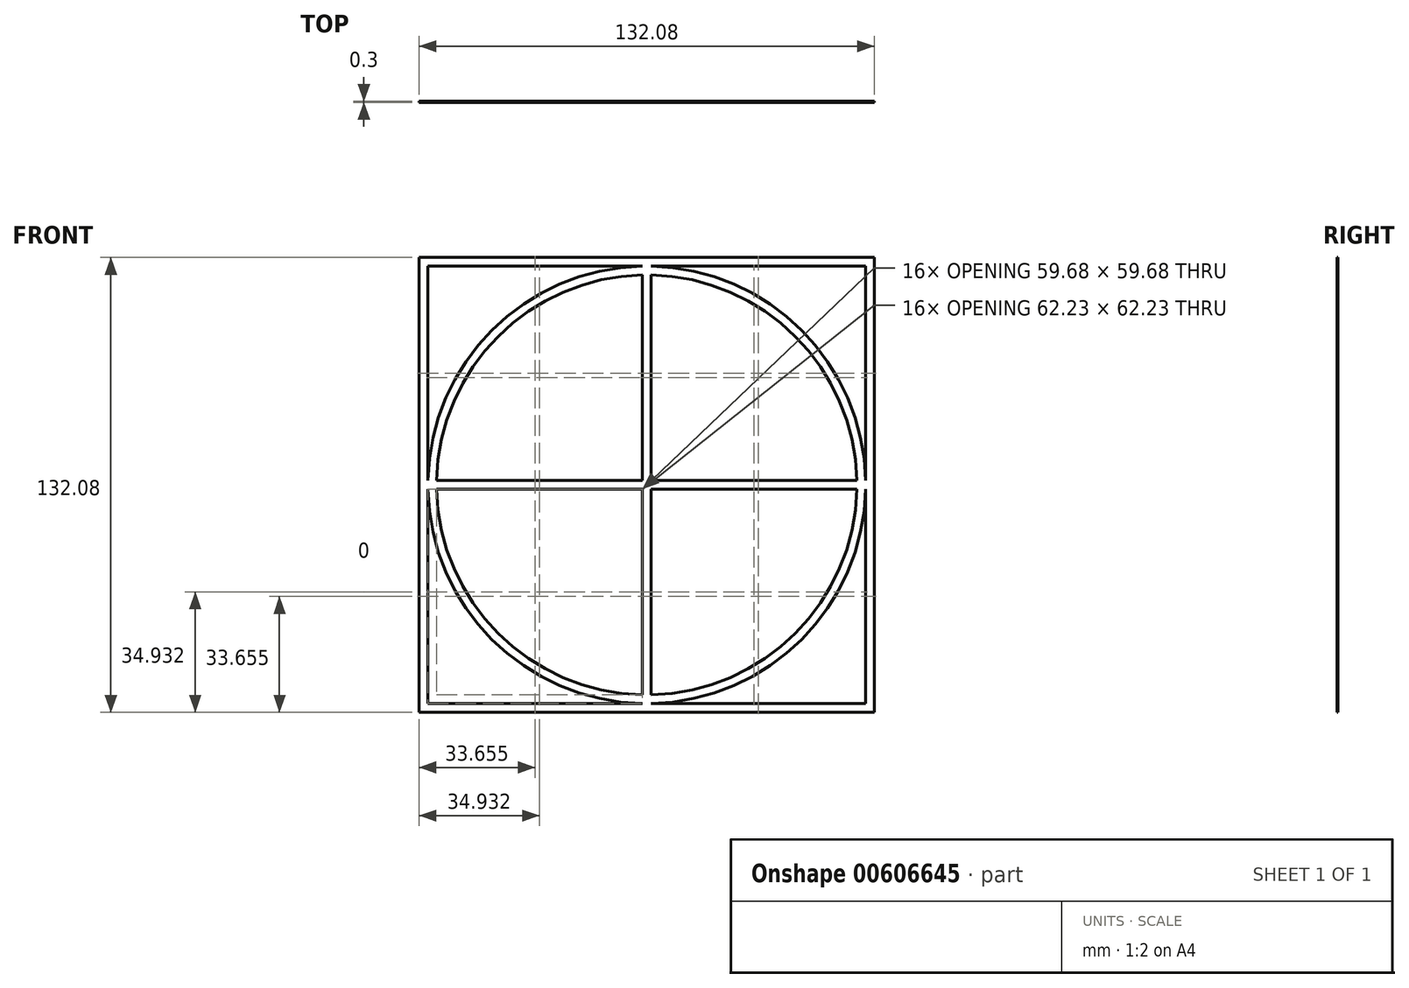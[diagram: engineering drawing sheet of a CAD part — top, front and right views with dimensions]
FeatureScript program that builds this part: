
annotation { "Feature Type Name" : "Feature", "Feature Type Description" : "" }
export const myFeature = defineFeature(function(context is Context, id is Id, definition is map)
    precondition{}
    {
        {
            var Q0;
            Q0=qCreatedBy(makeId("Front.planeOp"),FACE);
            var sketch = newSketch(context, id + "F0", { "sketchPlane" : qUnion([Q0])});
            skLineSegment(sketch, "E0.bottom", {"start": v(63.5, 63.5) * mm, "end": v(1.27, 63.5) * mm});
            skLineSegment(sketch, "E0.left", {"start": v(63.5, 63.5) * mm, "end": v(63.5, 1.27) * mm});
            skLineSegment(sketch, "E1.top", {"start": v(63.5, -63.5) * mm, "end": v(1.27, -63.5) * mm});
            skLineSegment(sketch, "E1.left", {"start": v(63.5, -1.27) * mm, "end": v(63.5, -63.5) * mm});
            skLineSegment(sketch, "E2.bottom", {"start": v(-1.27, -63.5) * mm, "end": v(-63.5, -63.5) * mm});
            skLineSegment(sketch, "E2.right", {"start": v(-63.5, -63.5) * mm, "end": v(-63.5, -1.27) * mm});
            skLineSegment(sketch, "E3.bottom", {"start": v(-1.27, 63.5) * mm, "end": v(-63.5, 63.5) * mm});
            skLineSegment(sketch, "E3.right", {"start": v(-63.5, 63.5) * mm, "end": v(-63.5, 1.27) * mm});
            skPoint(sketch, "E0.right.end.orphan", {"position": v(0, 0) * mm});
            skLineSegment(sketch, "E4.0", {"start": v(63.5, 1.27) * mm, "end": v(63.49, 1.27) * mm});
            skLineSegment(sketch, "E5.0", {"start": v(63.5, -1.27) * mm, "end": v(63.49, -1.27) * mm});
            skLineSegment(sketch, "E6.0", {"start": v(-1.27, 63.5) * mm, "end": v(-1.27, 63.49) * mm});
            skLineSegment(sketch, "E7.0", {"start": v(1.27, 63.5) * mm, "end": v(1.27, 63.49) * mm});
            skLineSegment(sketch, "E8.trimOffspring", {"start": v(1.27, -1.27) * mm, "end": v(1.27, -60.95) * mm});
            skLineSegment(sketch, "E9.trimOffspring", {"start": v(-1.27, 1.27) * mm, "end": v(-60.95, 1.27) * mm});
            skLineSegment(sketch, "E10.trimOffspring", {"start": v(-1.27, -1.27) * mm, "end": v(-1.27, -60.95) * mm});
            skLineSegment(sketch, "E11.trimOffspring", {"start": v(-1.27, -1.27) * mm, "end": v(-60.95, -1.27) * mm});
            skArc(sketch, "E12", {"start": v(-1.27, 63.49) * mm, "mid": v(-44.9, 44.9) * mm, "end": v(-63.49, 1.27) * mm});
            skLineSegment(sketch, "E13.0", {"start": v(66.04, 66.04) * mm, "end": v(66.04, 0) * mm});
            skLineSegment(sketch, "E13.1", {"start": v(66.04, 0) * mm, "end": v(66.04, -66.04) * mm});
            skLineSegment(sketch, "E13.2", {"start": v(66.04, 66.04) * mm, "end": v(0, 66.04) * mm});
            skLineSegment(sketch, "E13.3", {"start": v(66.04, -66.04) * mm, "end": v(0, -66.04) * mm});
            skLineSegment(sketch, "E13.4", {"start": v(0, 66.04) * mm, "end": v(-66.04, 66.04) * mm});
            skLineSegment(sketch, "E13.5", {"start": v(-66.04, 66.04) * mm, "end": v(-66.04, 0) * mm});
            skLineSegment(sketch, "E13.6", {"start": v(-66.04, -66.04) * mm, "end": v(-66.04, 0) * mm});
            skLineSegment(sketch, "E13.7", {"start": v(0, -66.04) * mm, "end": v(-66.04, -66.04) * mm});
            skArc(sketch, "E14.trimOffspring", {"start": v(63.49, 1.27) * mm, "mid": v(44.9, 44.9) * mm, "end": v(1.27, 63.49) * mm});
            skPoint(sketch, "E15.orphan", {"position": v(-63.5, 0) * mm});
            skArc(sketch, "E16.trimOffspring", {"start": v(-63.49, -1.27) * mm, "mid": v(-44.9, -44.9) * mm, "end": v(-1.27, -63.49) * mm});
            skArc(sketch, "E17.trimOffspring", {"start": v(1.27, -63.49) * mm, "mid": v(44.9, -44.9) * mm, "end": v(63.49, -1.27) * mm});
            skPoint(sketch, "E18.orphan", {"position": v(0, -63.5) * mm});
            skArc(sketch, "E19.0", {"start": v(-1.22, 60.95) * mm, "mid": v(-43.1, 43.1) * mm, "end": v(-60.95, 1.22) * mm});
            skArc(sketch, "E20.0", {"start": v(60.95, 1.22) * mm, "mid": v(43.1, 43.1) * mm, "end": v(1.22, 60.95) * mm});
            skArc(sketch, "E21.0", {"start": v(1.22, -60.95) * mm, "mid": v(43.1, -43.1) * mm, "end": v(60.95, -1.22) * mm});
            skArc(sketch, "E22.0", {"start": v(-60.95, -1.22) * mm, "mid": v(-43.1, -43.1) * mm, "end": v(-1.22, -60.95) * mm});
            skLineSegment(sketch, "E23.trimOffspring", {"start": v(-63.49, -1.27) * mm, "end": v(-63.5, -1.27) * mm});
            skLineSegment(sketch, "E24.trimOffspring", {"start": v(-63.49, 1.27) * mm, "end": v(-63.5, 1.27) * mm});
            skLineSegment(sketch, "E25.trimOffspring", {"start": v(-1.27, -63.49) * mm, "end": v(-1.27, -63.5) * mm});
            skLineSegment(sketch, "E26.trimOffspring", {"start": v(1.27, -63.49) * mm, "end": v(1.27, -63.5) * mm});
            skLineSegment(sketch, "E27.trimOffspring", {"start": v(-1.27, 60.95) * mm, "end": v(-1.27, 1.27) * mm});
            skLineSegment(sketch, "E28.trimOffspring", {"start": v(1.27, 60.95) * mm, "end": v(1.27, 1.27) * mm});
            skLineSegment(sketch, "E29.trimOffspring", {"start": v(60.95, -1.27) * mm, "end": v(1.27, -1.27) * mm});
            skLineSegment(sketch, "E30.trimOffspring", {"start": v(60.95, 1.27) * mm, "end": v(1.27, 1.27) * mm});
            skSolve(sketch);
        }
        {
            var Q0;
            Q0 = qSketchRegion(id + "F0", true);
            extrude(context, id + "F1", {"entities" : qUnion([Q0]), "depth" : 0.3 * mm, "offsetDistance" : 25.4 * mm});
        }
    });
